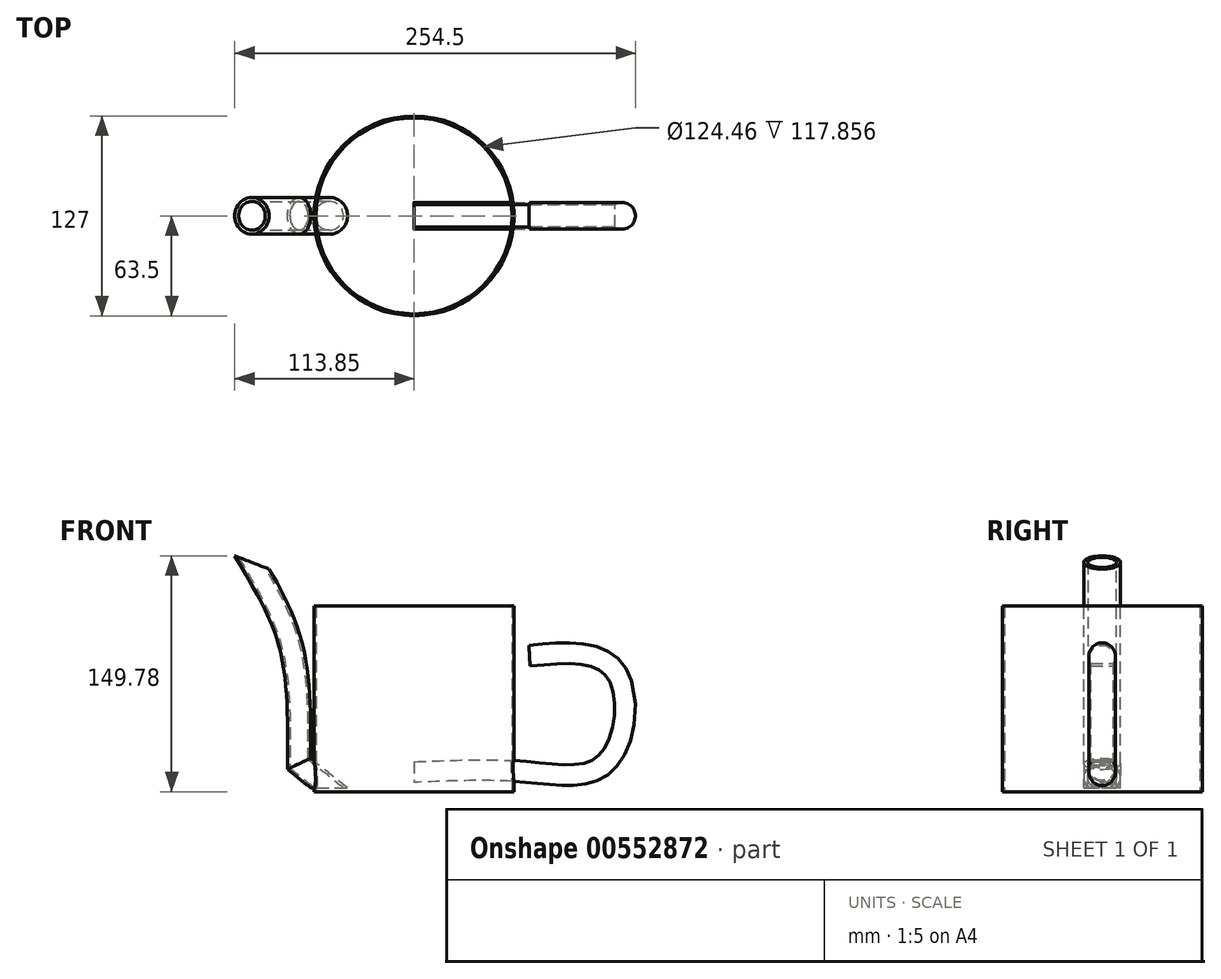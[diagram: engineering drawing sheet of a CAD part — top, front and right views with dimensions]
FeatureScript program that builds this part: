
annotation { "Feature Type Name" : "Feature", "Feature Type Description" : "" }
export const myFeature = defineFeature(function(context is Context, id is Id, definition is map)
    precondition{}
    {
        {
            var Q0;
            Q0=qCreatedBy(makeId("Front.planeOp"),FACE);
            var sketch = newSketch(context, id + "F0", { "sketchPlane" : qUnion([Q0])});
            skLineSegment(sketch, "E0", {"start": v(0, 0) * mm, "end": v(-63.5, 0) * mm});
            skFitSpline(sketch, "E1", {"points": [v(-63.5, 0) * mm, v(-100.62, 35.3) * mm, v(-102.14, 63.8) * mm, v(-93.5, 87.3) * mm, v(-65.5, 112.03) * mm, v(0, 140.89) * mm], "startDerivative": vector(-353.73, 113.25) * mm, "endDerivative": vector(484.18, -18.4) * mm});
            skLineSegment(sketch, "E2", {"start": v(0, 0) * mm, "end": v(0, 140.89) * mm});
            skSolve(sketch);
        }
        {
            var Q0;
            Q0=sQuery(id+"F0.wireOp",EDGE,"E1");
            var Q1;
            Q1=sQuery(id+"F0.wireOp",EDGE,"E0");
            var Q2;
            Q2=sQuery(id+"F0.wireOp",EDGE,"E2");
            revolve(context, id + "F1", {"bodyType" : ToolBodyType.SURFACE, "surfaceEntities" : qUnion([Q0, Q1]), "axis" : qUnion([Q2]), "revolveType" : RevolveType.FULL});
        }
        {
            var Q0;
            Q0=qCreatedBy(makeId("Top.planeOp"),FACE);
            var sketch = newSketch(context, id + "F2", { "sketchPlane" : qUnion([Q0])});
            skCircle(sketch, "E3", {"center": v(0, 0) * mm, "radius": 63.5 * mm});
            skCircle(sketch, "E4", {"center": v(0, 0) * mm, "radius": 62.23 * mm});
            skSolve(sketch);
        }
        {
            var Q0;
            Q0 = qSketchRegion(id + "F2", true);
            extrude(context, id + "F3", {"entities" : qUnion([Q0]), "depth" : 115.57 * mm, "offsetDistance" : 25.4 * mm, "hasSecondDirection" : true, "secondDirectionOppositeDirection" : true, "secondDirectionDepth" : 2.3 * mm});
        }
        {
            var Q0;
            Q0=qCreatedBy(makeId("Front.planeOp"),FACE);
            var sketch = newSketch(context, id + "F4", { "sketchPlane" : qUnion([Q0])});
            skLineSegment(sketch, "E5", {"start": v(0, 0) * mm, "end": v(-54.43, 0) * mm});
            skLineSegment(sketch, "E6", {"start": v(-54.43, 0) * mm, "end": v(-73.4, 15.28) * mm});
            skFitSpline(sketch, "E7", {"points": [v(-73.4, 15.28) * mm, v(-78.76, 89.92) * mm, v(-103.5, 143.53) * mm], "startDerivative": vector(1.12, 148.08) * mm, "endDerivative": vector(-62.59, 107.62) * mm});
            skSolve(sketch);
        }
        {
            var Q0;
            Q0=qCreatedBy(makeId("Top.planeOp"),FACE);
            var sketch = newSketch(context, id + "F5", { "sketchPlane" : qUnion([Q0])});
            skCircle(sketch, "E8", {"center": v(-53.83, 0) * mm, "radius": 11.68 * mm});
            skCircle(sketch, "E9", {"center": v(-53.83, 0) * mm, "radius": 9.1 * mm});
            skSolve(sketch);
        }
        {
            var Q0;
            Q0 = qSketchRegion(id + "F5", true);
            var Q1;
            Q1=sQuery(id+"F4.wireOp",EDGE,"E6");
            var Q2;
            Q2=sQuery(id+"F4.wireOp",EDGE,"E7");
            sweep(context, id + "F6", {"operationType" : NewBodyOperationType.ADD, "profiles" : qUnion([Q0]), "path" : qUnion([Q1, Q2])});
        }
        {
            var Q0;
            Q0=qCreatedBy(makeId("Front.planeOp"),FACE);
            var sketch = newSketch(context, id + "F7", { "sketchPlane" : qUnion([Q0])});
            skLineSegment(sketch, "E10", {"start": v(0, 0) * mm, "end": v(0, 12.5) * mm});
            skFitSpline(sketch, "E11", {"points": [v(0, 12.5) * mm, v(72.62, 12.5) * mm, v(121.04, 18.44) * mm, v(126.14, 72.8) * mm, v(73.47, 81.73) * mm], "startDerivative": vector(261.66, 10.92) * mm, "endDerivative": vector(-268.4, -26.44) * mm});
            skSolve(sketch);
        }
        {
            var Q0;
            Q0=qCreatedBy(makeId("Right.planeOp"),FACE);
            var sketch = newSketch(context, id + "F8", { "sketchPlane" : qUnion([Q0])});
            skArc(sketch, "E12", {"start": v(-7.08, 16.75) * mm, "mid": v(0, 3.59) * mm, "end": v(7.08, 16.75) * mm});
            skLineSegment(sketch, "E13", {"start": v(0, 12.07) * mm, "end": v(0, 16.75) * mm});
            skLineSegment(sketch, "E14", {"start": v(0, 16.75) * mm, "end": v(-7.08, 16.75) * mm});
            skLineSegment(sketch, "E15", {"start": v(0, 16.75) * mm, "end": v(7.08, 16.75) * mm});
            skSolve(sketch);
        }
        {
            var Q0;
            Q0 = qSketchRegion(id + "F8", true);
            var Q1;
            Q1=sQuery(id+"F7.wireOp",EDGE,"E11");
            sweep(context, id + "F9", {"operationType" : NewBodyOperationType.ADD, "profiles" : qUnion([Q0]), "path" : qUnion([Q1])});
        }
    });
